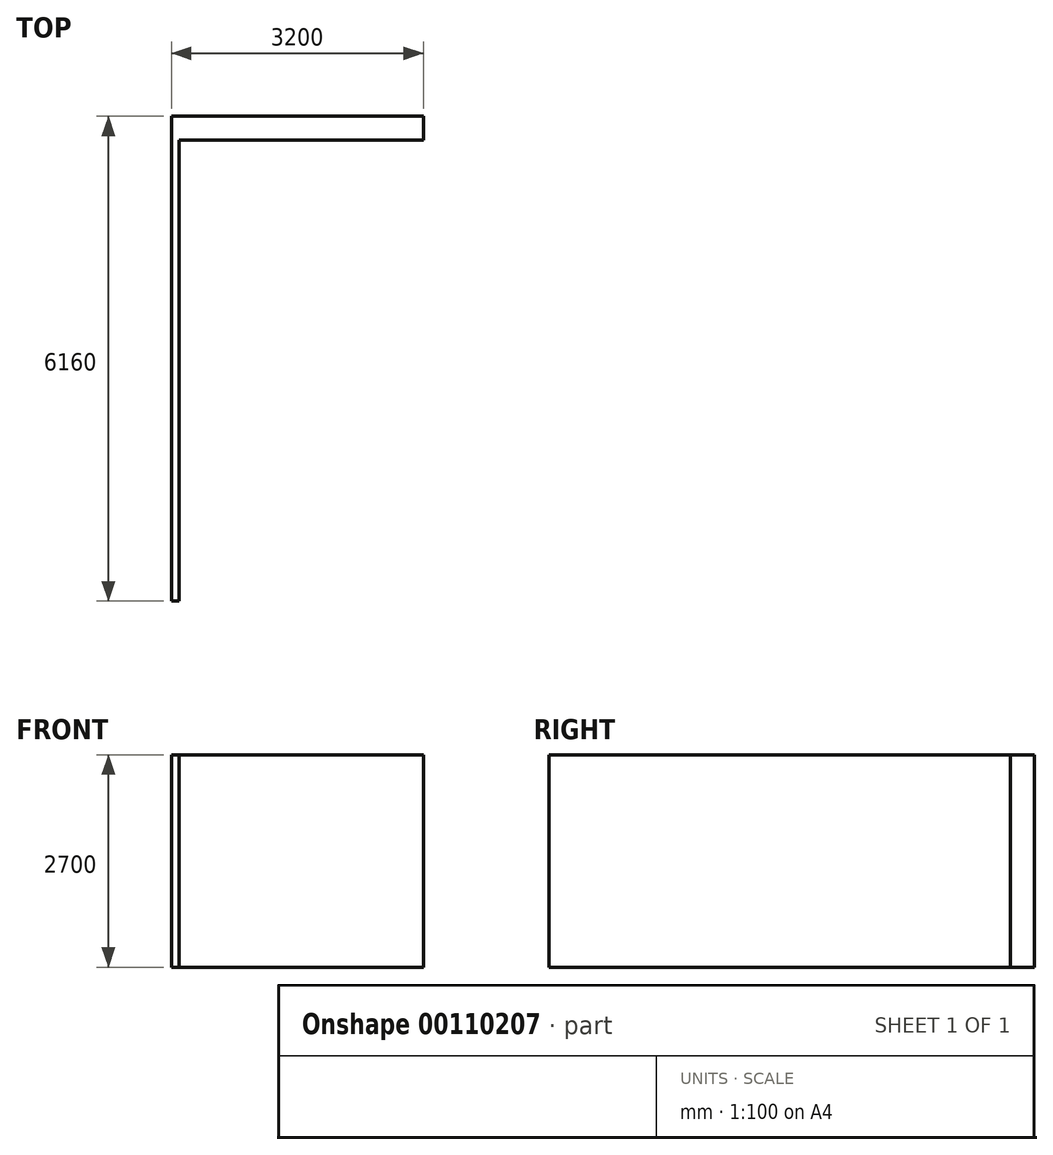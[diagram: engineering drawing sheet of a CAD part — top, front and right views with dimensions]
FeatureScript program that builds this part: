
annotation { "Feature Type Name" : "Feature", "Feature Type Description" : "" }
export const myFeature = defineFeature(function(context is Context, id is Id, definition is map)
    precondition{}
    {
        {
            var Q0;
            Q0=qCreatedBy(makeId("Top.planeOp"),FACE);
            var sketch = newSketch(context, id + "F0", { "sketchPlane" : qUnion([Q0])});
            skLineSegment(sketch, "E0.bottom", {"start": v(-1614.33, 4241.61) * mm, "end": v(1585.67, 4241.61) * mm});
            skLineSegment(sketch, "E0.top", {"start": v(-1614.33, -1918.39) * mm, "end": v(1585.67, -1918.39) * mm});
            skLineSegment(sketch, "E0.left", {"start": v(-1614.33, 4241.61) * mm, "end": v(-1614.33, -1918.39) * mm});
            skLineSegment(sketch, "E0.right", {"start": v(1585.67, 4241.61) * mm, "end": v(1585.67, -1918.39) * mm});
            skSolve(sketch);
        }
        {
            var Q0;
            Q0=makeQuery(id+"F0.imprint","IMPRINT",FACE,{"disambiguationData":[TD([[makeQuery(id+"F0.imprint","IMPRINT",EDGE,{"derivedFrom":sQuery(id+"F0.wireOp",EDGE,"E0.bottom")}),-1.0]])]});
            extrude(context, id + "F1", {"entities" : qUnion([Q0]), "depth" : 25 * mm});
        }
        {
            var Q0;
            Q0=makeQuery(id+"F1.opExtrude","CAP_FACE",FACE,{"disambiguationData":[OSD([sQuery(id+"F0.wireOp",EDGE,"E0.bottom"),sQuery(id+"F0.wireOp",EDGE,"E0.top"),sQuery(id+"F0.wireOp",EDGE,"E0.left"),sQuery(id+"F0.wireOp",EDGE,"E0.right")])],"isStart":false});
            var sketch = newSketch(context, id + "F2", { "sketchPlane" : qUnion([Q0])});
            skLineSegment(sketch, "E1.bottom", {"start": v(-1614.33, -1918.39) * mm, "end": v(-1514.33, -1918.39) * mm});
            skLineSegment(sketch, "E1.top", {"start": v(-1614.33, 4241.61) * mm, "end": v(-1514.33, 4241.61) * mm});
            skLineSegment(sketch, "E1.left", {"start": v(-1614.33, -1918.39) * mm, "end": v(-1614.33, 4241.61) * mm});
            skLineSegment(sketch, "E1.right", {"start": v(-1514.33, -1918.39) * mm, "end": v(-1514.33, 3941.61) * mm});
            skLineSegment(sketch, "E2.bottom", {"start": v(-1514.33, 4241.61) * mm, "end": v(1585.67, 4241.61) * mm});
            skLineSegment(sketch, "E2.top", {"start": v(-1514.33, 3941.61) * mm, "end": v(1585.67, 3941.61) * mm});
            skLineSegment(sketch, "E2.right", {"start": v(1585.67, 4241.61) * mm, "end": v(1585.67, 3941.61) * mm});
            skSolve(sketch);
        }
        {
            var Q0;
            Q0 = qSketchRegion(id + "F2", true);
            extrude(context, id + "F3", {"entities" : qUnion([Q0]), "operationType" : NewBodyOperationType.ADD, "depth" : 2700 * mm});
        }
        {
            var Q0;
            Q0=makeQuery(id+"F1.opExtrude","CAP_FACE",FACE,{"disambiguationData":[OSD([sQuery(id+"F0.wireOp",EDGE,"E0.bottom"),sQuery(id+"F0.wireOp",EDGE,"E0.top"),sQuery(id+"F0.wireOp",EDGE,"E0.left"),sQuery(id+"F0.wireOp",EDGE,"E0.right")])],"isStart":false});
            var sketch = newSketch(context, id + "F4", { "sketchPlane" : qUnion([Q0])});
            skLineSegment(sketch, "E3.bottom", {"start": v(-2076.59, 4675.74) * mm, "end": v(2788.26, 4675.74) * mm});
            skLineSegment(sketch, "E3.top", {"start": v(-2076.59, -2110.4) * mm, "end": v(2788.26, -2110.4) * mm});
            skLineSegment(sketch, "E3.left", {"start": v(-2076.59, 4675.74) * mm, "end": v(-2076.59, -2110.4) * mm});
            skLineSegment(sketch, "E3.right", {"start": v(2788.26, 4675.74) * mm, "end": v(2788.26, -2110.4) * mm});
            skSolve(sketch);
        }
        {
            var Q0;
            Q0 = qSketchRegion(id + "F4", true);
            extrude(context, id + "F5", {"entities" : qUnion([Q0]), "operationType" : NewBodyOperationType.REMOVE, "oppositeDirection" : true, "depth" : 350 * mm});
        }
    });
